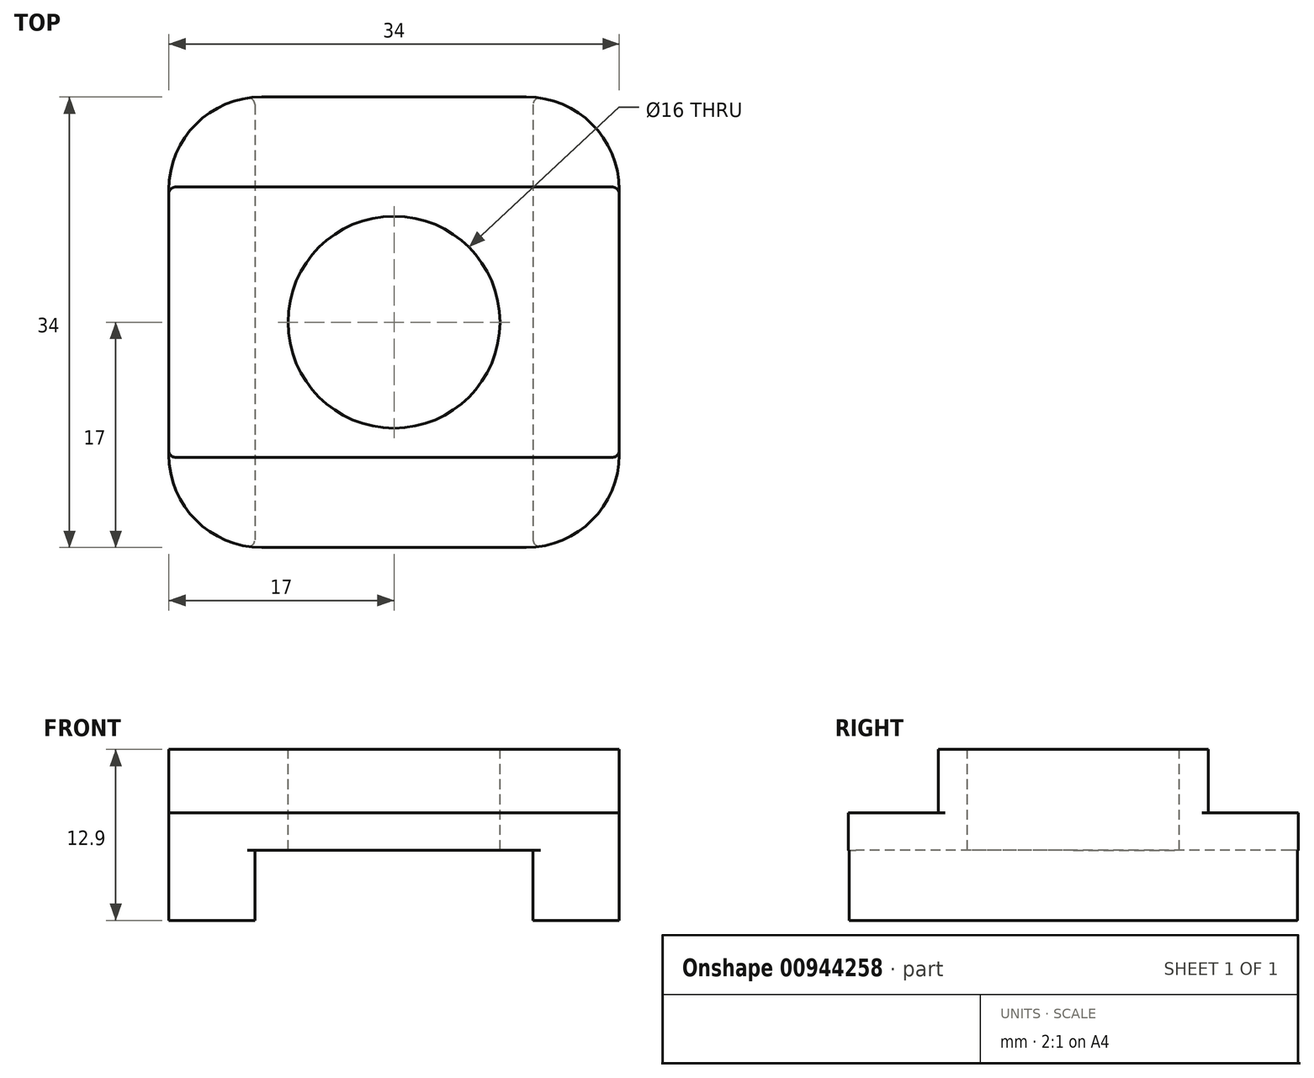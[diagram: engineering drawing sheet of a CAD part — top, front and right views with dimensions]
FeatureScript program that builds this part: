
annotation { "Feature Type Name" : "Feature", "Feature Type Description" : "" }
export const myFeature = defineFeature(function(context is Context, id is Id, definition is map)
    precondition{}
    {
        {
            var Q0;
            Q0=qCreatedBy(makeId("Top.planeOp"),FACE);
            var sketch = newSketch(context, id + "F0", { "sketchPlane" : qUnion([Q0])});
            skLineSegment(sketch, "E0.bottom", {"start": v(-17, 17) * mm, "end": v(17, 17) * mm});
            skLineSegment(sketch, "E0.top", {"start": v(-17, -17) * mm, "end": v(17, -17) * mm});
            skLineSegment(sketch, "E0.left", {"start": v(-17, 17) * mm, "end": v(-17, -17) * mm});
            skLineSegment(sketch, "E0.right", {"start": v(17, 17) * mm, "end": v(17, -17) * mm});
            skPoint(sketch, "E1", {"position": v(0, 17) * mm});
            skPoint(sketch, "E2", {"position": v(17, 0) * mm});
            skSolve(sketch);
        }
        {
            var Q0;
            Q0=qSketchRegion(id+"F0",true);
            extrude(context, id + "F1", {"entities" : qUnion([Q0]), "depth" : 12.9 * mm, "offsetDistance" : 25 * mm});
        }
        {
            var Q0;
            Q0=makeQuery(id+"F1.opExtrude","SWEPT_FACE",FACE,{"disambiguationData":[OSD([sQuery(id+"F0.wireOp",EDGE,"E0.top")])]});
            var sketch = newSketch(context, id + "F2", { "sketchPlane" : qUnion([Q0])});
            skLineSegment(sketch, "E3.bottom", {"start": v(-10.5, 0) * mm, "end": v(10.5, 0) * mm});
            skLineSegment(sketch, "E3.top", {"start": v(-10.5, 5.3) * mm, "end": v(10.5, 5.3) * mm});
            skLineSegment(sketch, "E3.left", {"start": v(-10.5, 0) * mm, "end": v(-10.5, 5.3) * mm});
            skLineSegment(sketch, "E3.right", {"start": v(10.5, 0) * mm, "end": v(10.5, 5.3) * mm});
            skPoint(sketch, "E4", {"position": v(0, 0) * mm});
            skSolve(sketch);
        }
        {
            var Q0;
            Q0=qSketchRegion(id+"F2",true);
            extrude(context, id + "F3", {"entities" : qUnion([Q0]), "operationType" : NewBodyOperationType.REMOVE, "endBound" : BoundingType.THROUGH_ALL, "oppositeDirection" : true, "depth" : 25 * mm, "offsetDistance" : 25 * mm});
        }
        {
            var Q0;
            Q0=makeQuery(id+"F1.opExtrude","SWEPT_FACE",FACE,{"disambiguationData":[OSD([sQuery(id+"F0.wireOp",EDGE,"E0.right")])]});
            var sketch = newSketch(context, id + "F4", { "sketchPlane" : qUnion([Q0])});
            skLineSegment(sketch, "E5.bottom", {"start": v(-17, 12.9) * mm, "end": v(-10.2, 12.9) * mm});
            skLineSegment(sketch, "E5.top", {"start": v(-17, 8.1) * mm, "end": v(-10.2, 8.1) * mm});
            skLineSegment(sketch, "E5.left", {"start": v(-17, 12.9) * mm, "end": v(-17, 8.1) * mm});
            skLineSegment(sketch, "E5.right", {"start": v(-10.2, 12.9) * mm, "end": v(-10.2, 8.1) * mm});
            skLineSegment(sketch, "E6.MirrorCS", {"start": v(17, 8.1) * mm, "end": v(10.2, 8.1) * mm});
            skLineSegment(sketch, "E7.MirrorCS", {"start": v(10.2, 12.9) * mm, "end": v(10.2, 8.1) * mm});
            skLineSegment(sketch, "E8.MirrorCS", {"start": v(17, 12.9) * mm, "end": v(17, 8.1) * mm});
            skLineSegment(sketch, "E9.MirrorCS", {"start": v(17, 12.9) * mm, "end": v(10.2, 12.9) * mm});
            skSolve(sketch);
        }
        {
            var Q0;
            Q0=qSketchRegion(id+"F4",true);
            extrude(context, id + "F5", {"entities" : qUnion([Q0]), "operationType" : NewBodyOperationType.REMOVE, "endBound" : BoundingType.THROUGH_ALL, "oppositeDirection" : true, "depth" : 25 * mm, "offsetDistance" : 25 * mm});
        }
        {
            var Q0;
            Q0=makeQuery(id+"F1.opExtrude","CAP_FACE",FACE,{"disambiguationData":[OSD([sQuery(id+"F0.wireOp",EDGE,"E0.bottom"),sQuery(id+"F0.wireOp",EDGE,"E0.top"),sQuery(id+"F0.wireOp",EDGE,"E0.left"),sQuery(id+"F0.wireOp",EDGE,"E0.right")])],"isStart":false});
            var sketch = newSketch(context, id + "F6", { "sketchPlane" : qUnion([Q0])});
            skCircle(sketch, "E10", {"center": v(0, 0) * mm, "radius": 8 * mm});
            skSolve(sketch);
        }
        {
            var Q0;
            Q0=qSketchRegion(id+"F6",true);
            extrude(context, id + "F7", {"entities" : qUnion([Q0]), "operationType" : NewBodyOperationType.REMOVE, "endBound" : BoundingType.THROUGH_ALL, "oppositeDirection" : true, "depth" : 25 * mm, "offsetDistance" : 25 * mm});
        }
        {
            var Q0;
            Q0=makeQuery(id+"F1.opExtrude","SWEPT_EDGE",EDGE,{"disambiguationData":[OSD([sQuery(id+"F0.wireOp",EDGE,"E0.top"),sQuery(id+"F0.wireOp",EDGE,"E0.right")])]});
            var Q1;
            Q1=makeQuery(id+"F1.opExtrude","SWEPT_EDGE",EDGE,{"disambiguationData":[OSD([sQuery(id+"F0.wireOp",EDGE,"E0.bottom"),sQuery(id+"F0.wireOp",EDGE,"E0.right")])]});
            var Q2;
            Q2=makeQuery(id+"F1.opExtrude","SWEPT_EDGE",EDGE,{"disambiguationData":[OSD([sQuery(id+"F0.wireOp",EDGE,"E0.top"),sQuery(id+"F0.wireOp",EDGE,"E0.left")])]});
            var Q3;
            Q3=makeQuery(id+"F1.opExtrude","SWEPT_EDGE",EDGE,{"disambiguationData":[OSD([sQuery(id+"F0.wireOp",EDGE,"E0.bottom"),sQuery(id+"F0.wireOp",EDGE,"E0.left")])]});
            fillet(context, id + "F8", {"entities" : qUnion([Q0, Q1, Q2, Q3]), "radius" : 7 * mm, "tangentPropagation" : true, "allowEdgeOverflow" : false});
        }
        {
            var Q0;
            Q0=makeQuery(id+"F8.opFillet","BLEND_EDGE",EDGE,{"blendedFrom":[makeQuery(id+"F1.opExtrude","SWEPT_EDGE",EDGE,{"disambiguationData":[OSD([sQuery(id+"F0.wireOp",EDGE,"E0.top"),sQuery(id+"F0.wireOp",EDGE,"E0.right")])]}),makeQuery(id+"F5.boolean.opBoolean","COPY",FACE,{"derivedFrom":makeQuery(id+"F5.opExtrude","SWEPT_FACE",FACE,{"disambiguationData":[OSD([sQuery(id+"F4.wireOp",EDGE,"E5.right")])]})})],"blendedInto":[makeQuery(id+"F5.boolean.opBoolean","COPY",FACE,{"derivedFrom":makeQuery(id+"F5.opExtrude","SWEPT_FACE",FACE,{"disambiguationData":[OSD([sQuery(id+"F4.wireOp",EDGE,"E5.right")])]})})]});
            var Q1;
            Q1=makeQuery(id+"F8.opFillet","BLEND_EDGE",EDGE,{"blendedFrom":[makeQuery(id+"F1.opExtrude","SWEPT_EDGE",EDGE,{"disambiguationData":[OSD([sQuery(id+"F0.wireOp",EDGE,"E0.bottom"),sQuery(id+"F0.wireOp",EDGE,"E0.right")])]}),makeQuery(id+"F5.boolean.opBoolean","COPY",FACE,{"derivedFrom":makeQuery(id+"F5.opExtrude","SWEPT_FACE",FACE,{"disambiguationData":[OSD([sQuery(id+"F4.wireOp",EDGE,"E7.MirrorCS")])]})})],"blendedInto":[makeQuery(id+"F5.boolean.opBoolean","COPY",FACE,{"derivedFrom":makeQuery(id+"F5.opExtrude","SWEPT_FACE",FACE,{"disambiguationData":[OSD([sQuery(id+"F4.wireOp",EDGE,"E7.MirrorCS")])]})})]});
            var Q2;
            Q2=makeQuery(id+"F8.opFillet","BLEND_EDGE",EDGE,{"blendedFrom":[makeQuery(id+"F1.opExtrude","SWEPT_EDGE",EDGE,{"disambiguationData":[OSD([sQuery(id+"F0.wireOp",EDGE,"E0.top"),sQuery(id+"F0.wireOp",EDGE,"E0.right")])]}),makeQuery(id+"F3.boolean.opBoolean","COPY",FACE,{"derivedFrom":makeQuery(id+"F3.opExtrude","SWEPT_FACE",FACE,{"disambiguationData":[OSD([sQuery(id+"F2.wireOp",EDGE,"E3.right")])]})})],"blendedInto":[makeQuery(id+"F3.boolean.opBoolean","COPY",FACE,{"derivedFrom":makeQuery(id+"F3.opExtrude","SWEPT_FACE",FACE,{"disambiguationData":[OSD([sQuery(id+"F2.wireOp",EDGE,"E3.right")])]})})]});
            var Q3;
            Q3=makeQuery(id+"F8.opFillet","BLEND_EDGE",EDGE,{"blendedFrom":[makeQuery(id+"F1.opExtrude","SWEPT_EDGE",EDGE,{"disambiguationData":[OSD([sQuery(id+"F0.wireOp",EDGE,"E0.top"),sQuery(id+"F0.wireOp",EDGE,"E0.left")])]}),makeQuery(id+"F3.boolean.opBoolean","COPY",FACE,{"derivedFrom":makeQuery(id+"F3.opExtrude","SWEPT_FACE",FACE,{"disambiguationData":[OSD([sQuery(id+"F2.wireOp",EDGE,"E3.left")])]})})],"blendedInto":[makeQuery(id+"F3.boolean.opBoolean","COPY",FACE,{"derivedFrom":makeQuery(id+"F3.opExtrude","SWEPT_FACE",FACE,{"disambiguationData":[OSD([sQuery(id+"F2.wireOp",EDGE,"E3.left")])]})})]});
            var Q4;
            Q4=makeQuery(id+"F8.opFillet","BLEND_EDGE",EDGE,{"blendedFrom":[makeQuery(id+"F1.opExtrude","SWEPT_EDGE",EDGE,{"disambiguationData":[OSD([sQuery(id+"F0.wireOp",EDGE,"E0.bottom"),sQuery(id+"F0.wireOp",EDGE,"E0.left")])]}),makeQuery(id+"F5.boolean.opBoolean","COPY",FACE,{"derivedFrom":makeQuery(id+"F5.opExtrude","SWEPT_FACE",FACE,{"disambiguationData":[OSD([sQuery(id+"F4.wireOp",EDGE,"E7.MirrorCS")])]})})],"blendedInto":[makeQuery(id+"F5.boolean.opBoolean","COPY",FACE,{"derivedFrom":makeQuery(id+"F5.opExtrude","SWEPT_FACE",FACE,{"disambiguationData":[OSD([sQuery(id+"F4.wireOp",EDGE,"E7.MirrorCS")])]})})]});
            var Q5;
            Q5=makeQuery(id+"F8.opFillet","BLEND_EDGE",EDGE,{"blendedFrom":[makeQuery(id+"F1.opExtrude","SWEPT_EDGE",EDGE,{"disambiguationData":[OSD([sQuery(id+"F0.wireOp",EDGE,"E0.bottom"),sQuery(id+"F0.wireOp",EDGE,"E0.left")])]}),makeQuery(id+"F3.boolean.opBoolean","COPY",FACE,{"derivedFrom":makeQuery(id+"F3.opExtrude","SWEPT_FACE",FACE,{"disambiguationData":[OSD([sQuery(id+"F2.wireOp",EDGE,"E3.left")])]})})],"blendedInto":[makeQuery(id+"F3.boolean.opBoolean","COPY",FACE,{"derivedFrom":makeQuery(id+"F3.opExtrude","SWEPT_FACE",FACE,{"disambiguationData":[OSD([sQuery(id+"F2.wireOp",EDGE,"E3.left")])]})})]});
            var Q6;
            Q6=makeQuery(id+"F8.opFillet","BLEND_EDGE",EDGE,{"blendedFrom":[makeQuery(id+"F1.opExtrude","SWEPT_EDGE",EDGE,{"disambiguationData":[OSD([sQuery(id+"F0.wireOp",EDGE,"E0.bottom"),sQuery(id+"F0.wireOp",EDGE,"E0.right")])]}),makeQuery(id+"F3.boolean.opBoolean","COPY",FACE,{"derivedFrom":makeQuery(id+"F3.opExtrude","SWEPT_FACE",FACE,{"disambiguationData":[OSD([sQuery(id+"F2.wireOp",EDGE,"E3.right")])]})})],"blendedInto":[makeQuery(id+"F3.boolean.opBoolean","COPY",FACE,{"derivedFrom":makeQuery(id+"F3.opExtrude","SWEPT_FACE",FACE,{"disambiguationData":[OSD([sQuery(id+"F2.wireOp",EDGE,"E3.right")])]})})]});
            var Q7;
            Q7=makeQuery(id+"F8.opFillet","BLEND_EDGE",EDGE,{"blendedFrom":[makeQuery(id+"F1.opExtrude","SWEPT_EDGE",EDGE,{"disambiguationData":[OSD([sQuery(id+"F0.wireOp",EDGE,"E0.top"),sQuery(id+"F0.wireOp",EDGE,"E0.left")])]}),makeQuery(id+"F5.boolean.opBoolean","COPY",FACE,{"derivedFrom":makeQuery(id+"F5.opExtrude","SWEPT_FACE",FACE,{"disambiguationData":[OSD([sQuery(id+"F4.wireOp",EDGE,"E5.right")])]})})],"blendedInto":[makeQuery(id+"F5.boolean.opBoolean","COPY",FACE,{"derivedFrom":makeQuery(id+"F5.opExtrude","SWEPT_FACE",FACE,{"disambiguationData":[OSD([sQuery(id+"F4.wireOp",EDGE,"E5.right")])]})})]});
            fillet(context, id + "F9", {"entities" : qUnion([Q0, Q1, Q2, Q3, Q4, Q5, Q6, Q7]), "radius" : 0.5 * mm, "tangentPropagation" : true, "allowEdgeOverflow" : false});
        }
    });
